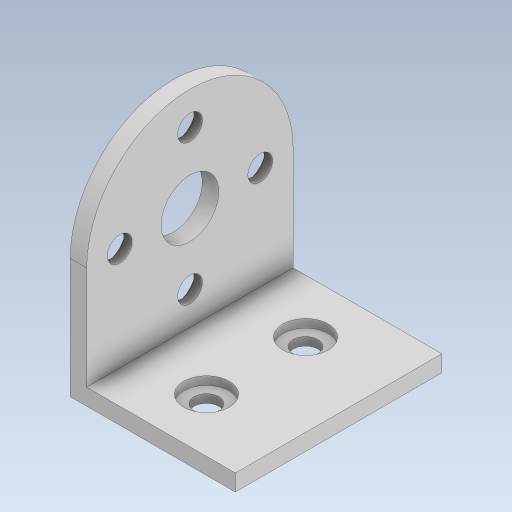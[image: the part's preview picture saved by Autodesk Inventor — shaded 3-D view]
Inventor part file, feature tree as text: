
AUTODESK INVENTOR PART (.ipt)
format: ipt  version: 2023.5 (Build 275446000, 446)  size: 383,488 bytes
history: native  units: in
note: dims shown in document units (in); Inventor stores cm internally (conversion verified against a paired STEP export)
features: extrude x7, sketch x3
ambient origin geometry x8: Origin, YZ Plane, XZ Plane, XY Plane, X Axis, Y Axis, Z Axis, Center Point
bodies: Solid1 (feature_tree)
feature tree (10):
  sketch  "Sketch1"  dims[d0=0.7874in d1=0.9843in]
  extrude  "Extrusion1"  Depth=0.9843in
  extrude  "Extrusion2"  Depth=0.0787in
  extrude  "Extrusion3"  Depth=0.2362in
  extrude  "Extrusion4"  Depth=0.0787in TaperAngle=0.0deg
  sketch  "Sketch3"  dims[d4=0.2165in d5=0.2362in d6=0.0787in d7=0.0in d8=0.0394in d9=0.0in d10=1.063in d11=0.0in d12=0.9843in d13=0.0787in d14=0.0in d15=0.1181in d16=0.2165in d17=0.3346in d18=0.0787in d19=0.0in d20=0.0394in d21=0.0in d22=0.2756in d23=0.0787in d24=0.0in d25=0.1181in d26=0.2165in d27=0.3346in d28=0.1181in d29=0.2165in d30=0.3346in]
  extrude  "Extrusion5"  Depth=0.0394in TaperAngle=0.0deg
  extrude  "Extrusion6"  Depth=0.0787in TaperAngle=0.0deg
  extrude  "Extrusion7"  Depth=0.9843in
  sketch  "Sketch2"  dims[d2=0.0787in d3=0.1181in]
